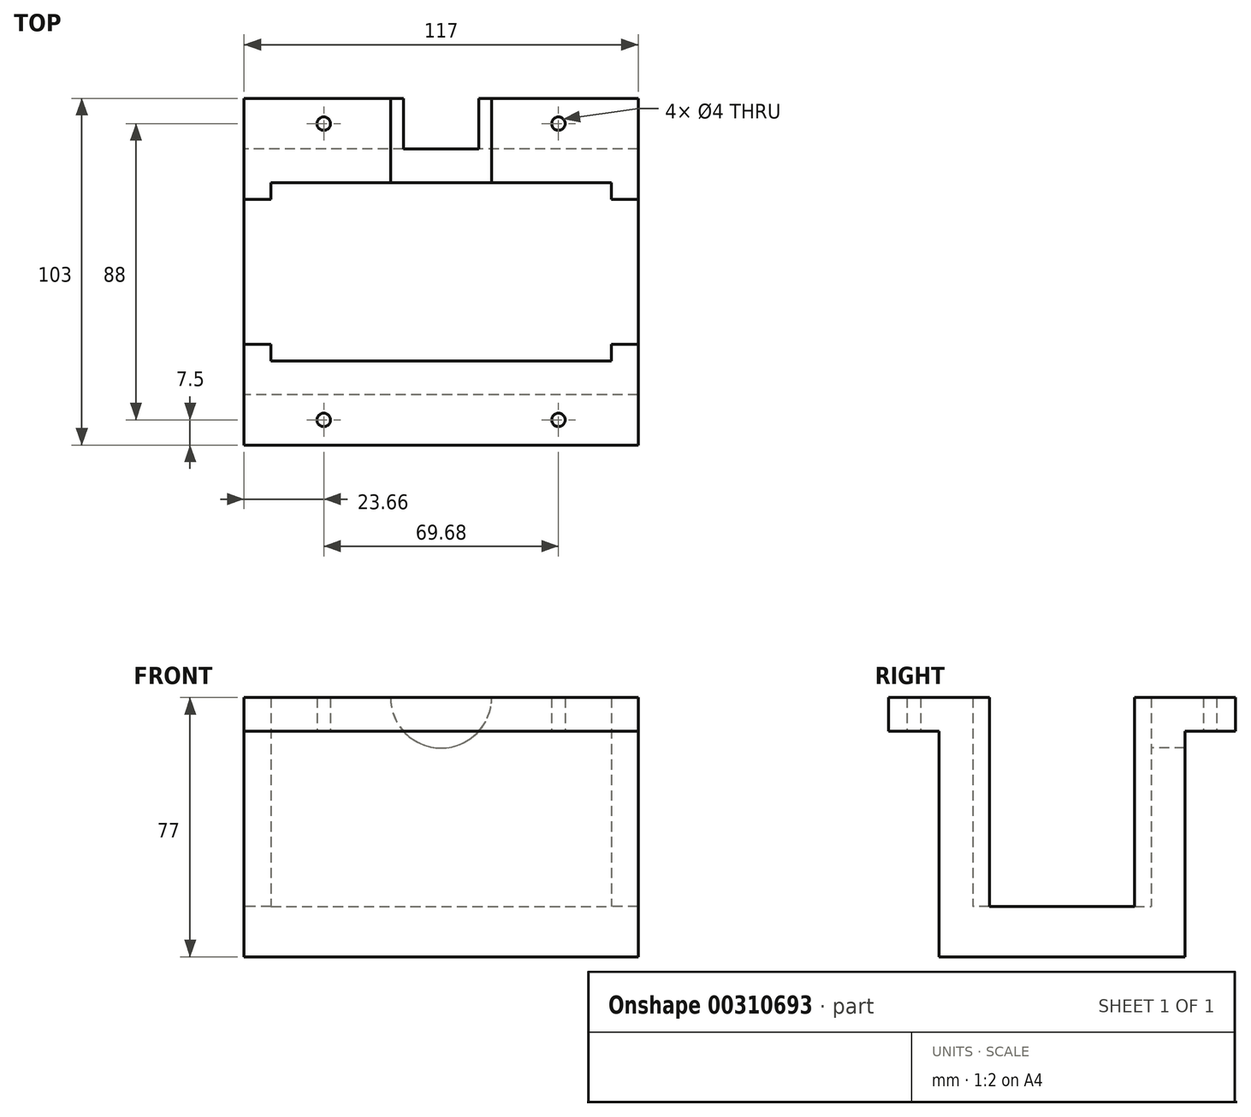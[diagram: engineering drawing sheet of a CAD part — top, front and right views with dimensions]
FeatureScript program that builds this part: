
annotation { "Feature Type Name" : "Feature", "Feature Type Description" : "" }
export const myFeature = defineFeature(function(context is Context, id is Id, definition is map)
    precondition{}
    {
        {
            var Q0;
            Q0=qCreatedBy(makeId("Right.planeOp"),FACE);
            var sketch = newSketch(context, id + "F0", { "sketchPlane" : qUnion([Q0])});
            skLineSegment(sketch, "E0.bottom", {"start": v(36.5, 23) * mm, "end": v(21.5, 23) * mm});
            skLineSegment(sketch, "E0.top", {"start": v(36.5, -23) * mm, "end": v(-36.5, -23) * mm});
            skLineSegment(sketch, "E0.left", {"start": v(36.5, 13) * mm, "end": v(36.5, -23) * mm});
            skLineSegment(sketch, "E0.right", {"start": v(-36.5, 13) * mm, "end": v(-36.5, -23) * mm});
            skPoint(sketch, "E0.middle", {"position": v(0, 0) * mm});
            skLineSegment(sketch, "E1.bottom", {"start": v(-36.5, 23) * mm, "end": v(-51.5, 23) * mm});
            skLineSegment(sketch, "E1.top", {"start": v(-36.5, 13) * mm, "end": v(-51.5, 13) * mm});
            skLineSegment(sketch, "E1.right", {"start": v(-51.5, 23) * mm, "end": v(-51.5, 13) * mm});
            skLineSegment(sketch, "E2.MirrorCS", {"start": v(36.5, 23) * mm, "end": v(51.5, 23) * mm});
            skLineSegment(sketch, "E3.MirrorCS", {"start": v(51.5, 23) * mm, "end": v(51.5, 13) * mm});
            skLineSegment(sketch, "E4.MirrorCS", {"start": v(36.5, 13) * mm, "end": v(51.5, 13) * mm});
            skLineSegment(sketch, "E5", {"start": v(-21.5, 23) * mm, "end": v(-21.5, -8) * mm});
            skLineSegment(sketch, "E6", {"start": v(-21.5, -8) * mm, "end": v(0, -8) * mm});
            skLineSegment(sketch, "E7.MirrorCS", {"start": v(21.5, 23) * mm, "end": v(21.5, -8) * mm});
            skLineSegment(sketch, "E8.MirrorCS", {"start": v(21.5, -8) * mm, "end": v(0, -8) * mm});
            skLineSegment(sketch, "E9.trimOffspring", {"start": v(-21.5, 23) * mm, "end": v(-36.5, 23) * mm});
            skSolve(sketch);
        }
        {
            var Q0;
            Q0 = qSketchRegion(id + "F0", true);
            extrude(context, id + "F1", {"entities" : qUnion([Q0]), "endBound" : BoundingType.SYMMETRIC, "depth" : 117 * mm});
        }
        {
            var Q0;
            Q0=qCreatedBy(makeId("Front.planeOp"),FACE);
            var sketch = newSketch(context, id + "F2", { "sketchPlane" : qUnion([Q0])});
            skLineSegment(sketch, "E10.0", {"start": v(58.5, 23) * mm, "end": v(-58.5, 23) * mm});
            skArc(sketch, "E11", {"start": v(-15, 23) * mm, "mid": v(0, 8) * mm, "end": v(15, 23) * mm});
            skLineSegment(sketch, "E12", {"start": v(-15, 23) * mm, "end": v(15, 23) * mm});
            skPoint(sketch, "E13.0.start.orphan", {"position": v(-58.5, 13) * mm});
            skPoint(sketch, "E14.0.start.orphan", {"position": v(58.5, 13) * mm});
            skPoint(sketch, "E15.0.end.orphan", {"position": v(-58.5, -23) * mm});
            skPoint(sketch, "E15.0.start.orphan", {"position": v(58.5, -23) * mm});
            skSolve(sketch);
        }
        {
            var Q0;
            Q0=makeQuery(id+"F2.imprint","IMPRINT",FACE,{"disambiguationData":[TD([[makeQuery(id+"F2.imprint","IMPRINT",EDGE,{"derivedFrom":sQuery(id+"F2.wireOp",EDGE,"E11")}),1.0]])]});
            extrude(context, id + "F3", {"entities" : qUnion([Q0]), "operationType" : NewBodyOperationType.REMOVE, "oppositeDirection" : true, "depth" : 136.4 * mm});
        }
        {
            var Q0;
            Q0=qCreatedBy(makeId("Top.planeOp"),FACE);
            var sketch = newSketch(context, id + "F4", { "sketchPlane" : qUnion([Q0])});
            skCircle(sketch, "E16", {"center": v(-34.84, -44) * mm, "radius": 2 * mm});
            skCircle(sketch, "E17.MirrorC", {"center": v(34.84, -44) * mm, "radius": 2 * mm});
            skCircle(sketch, "E18.MirrorC", {"center": v(-34.84, 44) * mm, "radius": 2 * mm});
            skCircle(sketch, "E19.MirrorC", {"center": v(34.84, 44) * mm, "radius": 2 * mm});
            skPoint(sketch, "E20.0.end.orphan", {"position": v(-11.18, -36.5) * mm});
            skPoint(sketch, "E20.0.start.orphan", {"position": v(-11.18, -51.5) * mm});
            skPoint(sketch, "E21.orphan", {"position": v(-58.5, -36.5) * mm});
            skPoint(sketch, "E22.0.end.orphan", {"position": v(-58.5, -51.5) * mm});
            skPoint(sketch, "E23.0.start.orphan", {"position": v(58.5, -36.5) * mm});
            skSolve(sketch);
        }
        {
            var Q0;
            Q0 = qSketchRegion(id + "F4", true);
            extrude(context, id + "F5", {"entities" : qUnion([Q0]), "operationType" : NewBodyOperationType.REMOVE, "depth" : 25 * mm});
        }
        {
            var Q0;
            Q0=qCreatedBy(makeId("Right.planeOp"),FACE);
            var sketch = newSketch(context, id + "F6", { "sketchPlane" : qUnion([Q0])});
            skLineSegment(sketch, "E24.0", {"start": v(-21.5, 23) * mm, "end": v(-21.5, -8) * mm});
            skLineSegment(sketch, "E25.0", {"start": v(-21.5, 23) * mm, "end": v(-26.5, 23) * mm});
            skLineSegment(sketch, "E26", {"start": v(-26.5, 23) * mm, "end": v(-26.5, -8) * mm});
            skLineSegment(sketch, "E27", {"start": v(-21.5, -8) * mm, "end": v(-26.5, -8) * mm});
            skPoint(sketch, "E28.orphan", {"position": v(-51.5, 23) * mm});
            skLineSegment(sketch, "E29.MirrorCS", {"start": v(21.5, 23) * mm, "end": v(21.5, -8) * mm});
            skLineSegment(sketch, "E30.MirrorCS", {"start": v(21.5, 23) * mm, "end": v(26.5, 23) * mm});
            skLineSegment(sketch, "E31.MirrorCS", {"start": v(21.5, -8) * mm, "end": v(26.5, -8) * mm});
            skLineSegment(sketch, "E32.MirrorCS", {"start": v(26.5, 23) * mm, "end": v(26.5, -8) * mm});
            skSolve(sketch);
        }
        {
            var Q0;
            Q0 = qSketchRegion(id + "F6", true);
            extrude(context, id + "F7", {"entities" : qUnion([Q0]), "operationType" : NewBodyOperationType.REMOVE, "endBound" : BoundingType.SYMMETRIC, "oppositeDirection" : true, "depth" : 101 * mm});
        }
        {
            var Q0;
            Q0=makeQuery(id+"F1.opExtrude","SWEPT_FACE",FACE,{"disambiguationData":[OSD([sQuery(id+"F0.wireOp",EDGE,"E0.top")])]});
            var sketch = newSketch(context, id + "F8", { "sketchPlane" : qUnion([Q0])});
            skLineSegment(sketch, "E33.bottom", {"start": v(-58.5, 36.5) * mm, "end": v(58.5, 36.5) * mm});
            skLineSegment(sketch, "E33.top", {"start": v(-58.5, -36.5) * mm, "end": v(58.5, -36.5) * mm});
            skLineSegment(sketch, "E33.left", {"start": v(-58.5, 36.5) * mm, "end": v(-58.5, -36.5) * mm});
            skLineSegment(sketch, "E33.right", {"start": v(58.5, 36.5) * mm, "end": v(58.5, -36.5) * mm});
            skSolve(sketch);
        }
        {
            var Q0;
            Q0=makeQuery(id+"F8.imprint","IMPRINT",FACE,{"disambiguationData":[TD([[makeQuery(id+"F8.imprint","IMPRINT",EDGE,{"derivedFrom":sQuery(id+"F8.wireOp",EDGE,"E33.bottom")}),1.0]])]});
            extrude(context, id + "F9", {"entities" : qUnion([Q0]), "operationType" : NewBodyOperationType.ADD, "depth" : 31 * mm});
        }
        {
            var Q0;
            Q0=makeQuery(id+"F7.boolean.opBoolean","MERGE",FACE,{"derivedFrom":[makeQuery(id+"F1.opExtrude","SWEPT_FACE",FACE,{"disambiguationData":[OSD([sQuery(id+"F0.wireOp",EDGE,"E6"),sQuery(id+"F0.wireOp",EDGE,"E8.MirrorCS")])]}),makeQuery(id+"F7.opExtrude","SWEPT_FACE",FACE,{"disambiguationData":[OSD([sQuery(id+"F6.wireOp",EDGE,"E27")])]}),makeQuery(id+"F7.opExtrude","SWEPT_FACE",FACE,{"disambiguationData":[OSD([sQuery(id+"F6.wireOp",EDGE,"E31.MirrorCS")])]})]});
            var sketch = newSketch(context, id + "F10", { "sketchPlane" : qUnion([Q0])});
            skLineSegment(sketch, "E34", {"start": v(-58.5, 21.5) * mm, "end": v(-50.5, 21.5) * mm});
            skLineSegment(sketch, "E35", {"start": v(-50.5, 21.5) * mm, "end": v(-50.5, 26.5) * mm});
            skLineSegment(sketch, "E36", {"start": v(-50.5, 26.5) * mm, "end": v(50.5, 26.5) * mm});
            skLineSegment(sketch, "E37", {"start": v(50.5, 26.5) * mm, "end": v(50.5, 21.5) * mm});
            skLineSegment(sketch, "E38", {"start": v(50.5, 21.5) * mm, "end": v(58.5, 21.5) * mm});
            skLineSegment(sketch, "E39", {"start": v(58.5, 21.5) * mm, "end": v(58.5, -21.5) * mm});
            skLineSegment(sketch, "E40", {"start": v(58.5, -21.5) * mm, "end": v(50.5, -21.5) * mm});
            skLineSegment(sketch, "E41", {"start": v(50.5, -21.5) * mm, "end": v(50.5, -26.5) * mm});
            skLineSegment(sketch, "E42", {"start": v(50.5, -26.5) * mm, "end": v(-50.5, -26.5) * mm});
            skLineSegment(sketch, "E43", {"start": v(-50.5, -26.5) * mm, "end": v(-50.5, -21.5) * mm});
            skLineSegment(sketch, "E44", {"start": v(-50.5, -21.5) * mm, "end": v(-58.5, -21.5) * mm});
            skLineSegment(sketch, "E45", {"start": v(-58.5, -21.5) * mm, "end": v(-58.5, 21.5) * mm});
            skSolve(sketch);
        }
        {
            var Q0;
            Q0 = qSketchRegion(id + "F10", true);
            extrude(context, id + "F11", {"entities" : qUnion([Q0]), "operationType" : NewBodyOperationType.REMOVE, "oppositeDirection" : true, "depth" : 31 * mm});
        }
    });
